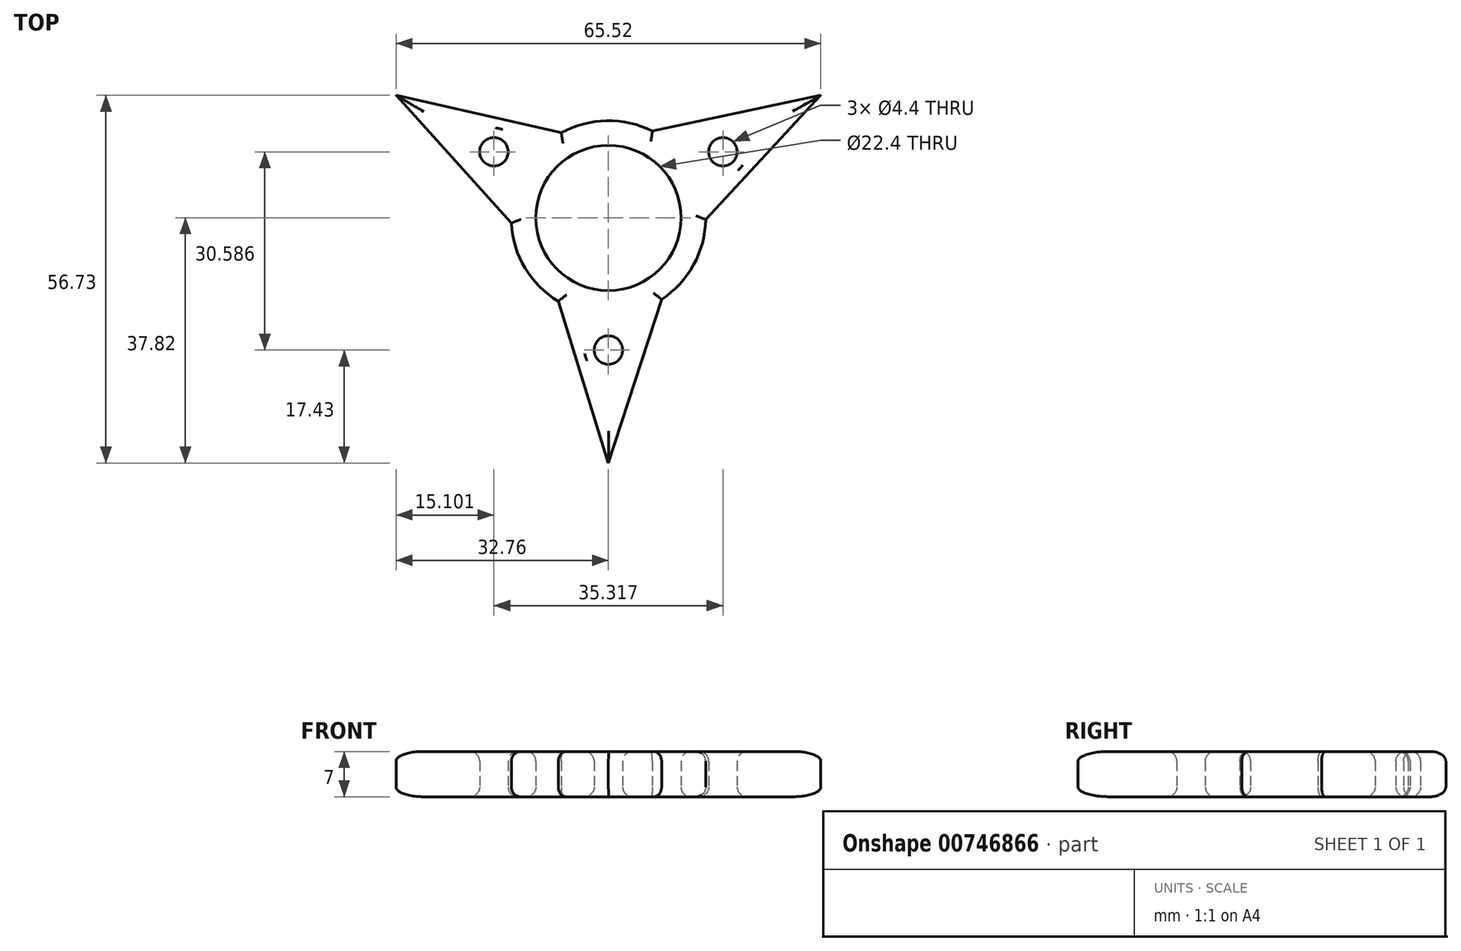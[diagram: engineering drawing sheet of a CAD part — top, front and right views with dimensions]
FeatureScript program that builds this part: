
annotation { "Feature Type Name" : "Feature", "Feature Type Description" : "" }
export const myFeature = defineFeature(function(context is Context, id is Id, definition is map)
    precondition{}
    {
        {
            var Q0;
            Q0=qCreatedBy(makeId("Top.planeOp"),FACE);
            var sketch = newSketch(context, id + "F0", { "sketchPlane" : qUnion([Q0])});
            skCircle(sketch, "E0", {"center": v(0, 0) * mm, "radius": 11.2 * mm});
            skArc(sketch, "E1", {"start": v(-14.98, -0.82) * mm, "mid": v(-12.85, -7.74) * mm, "end": v(-7.73, -12.86) * mm});
            skLineSegment(sketch, "E2", {"start": v(-7.73, -12.86) * mm, "end": v(0, -37.82) * mm});
            skLineSegment(sketch, "E3", {"start": v(0, -37.82) * mm, "end": v(8.2, -12.56) * mm});
            skLineSegment(sketch, "E4.1.0", {"start": v(15, -0.27) * mm, "end": v(32.76, 18.91) * mm});
            skLineSegment(sketch, "E4.1.1", {"start": v(32.76, 18.91) * mm, "end": v(6.78, 13.38) * mm});
            skLineSegment(sketch, "E4.2.0", {"start": v(-7.27, 13.12) * mm, "end": v(-32.76, 18.91) * mm});
            skLineSegment(sketch, "E4.2.1", {"start": v(-32.76, 18.91) * mm, "end": v(-14.98, -0.82) * mm});
            skCircle(sketch, "E5", {"center": v(0, -20.4) * mm, "radius": 2.2 * mm});
            skCircle(sketch, "E6.1.0", {"center": v(17.66, 10.2) * mm, "radius": 2.2 * mm});
            skCircle(sketch, "E6.2.0", {"center": v(-17.66, 10.2) * mm, "radius": 2.2 * mm});
            skArc(sketch, "E7.trimOffspring", {"start": v(8.2, -12.56) * mm, "mid": v(13.13, -7.26) * mm, "end": v(15, -0.27) * mm});
            skArc(sketch, "E8.trimOffspring", {"start": v(6.78, 13.38) * mm, "mid": v(-0.28, 15) * mm, "end": v(-7.27, 13.12) * mm});
            skSolve(sketch);
        }
        {
            var Q0;
            Q0=makeQuery(id+"F0.imprint","IMPRINT",FACE,{"disambiguationData":[TD([[makeQuery(id+"F0.imprint","IMPRINT",EDGE,{"derivedFrom":sQuery(id+"F0.wireOp",EDGE,"E0")}),-1.0]])]});
            extrude(context, id + "F1", {"entities" : qUnion([Q0]), "depth" : 7 * mm, "offsetDistance" : 25 * mm});
        }
        {
            var Q0;
            Q0=makeQuery(id+"F1.opExtrude","CAP_FACE",FACE,{"disambiguationData":[OSD([sQuery(id+"F0.wireOp",EDGE,"E0"),sQuery(id+"F0.wireOp",EDGE,"E1"),sQuery(id+"F0.wireOp",EDGE,"E2"),sQuery(id+"F0.wireOp",EDGE,"E3"),sQuery(id+"F0.wireOp",EDGE,"E4.1.0"),sQuery(id+"F0.wireOp",EDGE,"E4.1.1"),sQuery(id+"F0.wireOp",EDGE,"E4.2.0"),sQuery(id+"F0.wireOp",EDGE,"E4.2.1"),sQuery(id+"F0.wireOp",EDGE,"E5"),sQuery(id+"F0.wireOp",EDGE,"E6.1.0"),sQuery(id+"F0.wireOp",EDGE,"E6.2.0"),sQuery(id+"F0.wireOp",EDGE,"E7.trimOffspring"),sQuery(id+"F0.wireOp",EDGE,"E8.trimOffspring")])],"isStart":false});
            var Q1;
            Q1=makeQuery(id+"F1.opExtrude","CAP_FACE",FACE,{"disambiguationData":[OSD([sQuery(id+"F0.wireOp",EDGE,"E0"),sQuery(id+"F0.wireOp",EDGE,"E1"),sQuery(id+"F0.wireOp",EDGE,"E2"),sQuery(id+"F0.wireOp",EDGE,"E3"),sQuery(id+"F0.wireOp",EDGE,"E4.1.0"),sQuery(id+"F0.wireOp",EDGE,"E4.1.1"),sQuery(id+"F0.wireOp",EDGE,"E4.2.0"),sQuery(id+"F0.wireOp",EDGE,"E4.2.1"),sQuery(id+"F0.wireOp",EDGE,"E5"),sQuery(id+"F0.wireOp",EDGE,"E6.1.0"),sQuery(id+"F0.wireOp",EDGE,"E6.2.0"),sQuery(id+"F0.wireOp",EDGE,"E7.trimOffspring"),sQuery(id+"F0.wireOp",EDGE,"E8.trimOffspring")])],"isStart":true});
            var Q2;
            Q2=makeQuery(id+"F1.opExtrude","CAP_EDGE",EDGE,{"disambiguationData":[OSD([sQuery(id+"F0.wireOp",EDGE,"E2")])],"isStart":true});
            var Q3;
            Q3=makeQuery(id+"F1.opExtrude","CAP_EDGE",EDGE,{"disambiguationData":[OSD([sQuery(id+"F0.wireOp",EDGE,"E1")])],"isStart":true});
            var Q4;
            Q4=makeQuery(id+"F1.opExtrude","CAP_EDGE",EDGE,{"disambiguationData":[OSD([sQuery(id+"F0.wireOp",EDGE,"E4.2.1")])],"isStart":true});
            var Q5;
            Q5=makeQuery(id+"F1.opExtrude","CAP_EDGE",EDGE,{"disambiguationData":[OSD([sQuery(id+"F0.wireOp",EDGE,"E4.2.0")])],"isStart":true});
            var Q6;
            Q6=makeQuery(id+"F1.opExtrude","CAP_EDGE",EDGE,{"disambiguationData":[OSD([sQuery(id+"F0.wireOp",EDGE,"E6.2.0")])],"isStart":true});
            var Q7;
            Q7=makeQuery(id+"F1.opExtrude","CAP_EDGE",EDGE,{"disambiguationData":[OSD([sQuery(id+"F0.wireOp",EDGE,"E5")])],"isStart":true});
            var Q8;
            Q8=makeQuery(id+"F1.opExtrude","CAP_EDGE",EDGE,{"disambiguationData":[OSD([sQuery(id+"F0.wireOp",EDGE,"E6.1.0")])],"isStart":true});
            var Q9;
            Q9=makeQuery(id+"F1.opExtrude","CAP_EDGE",EDGE,{"disambiguationData":[OSD([sQuery(id+"F0.wireOp",EDGE,"E8.trimOffspring")])],"isStart":true});
            var Q10;
            Q10=makeQuery(id+"F1.opExtrude","CAP_EDGE",EDGE,{"disambiguationData":[OSD([sQuery(id+"F0.wireOp",EDGE,"E4.1.1")])],"isStart":true});
            var Q11;
            Q11=makeQuery(id+"F1.opExtrude","CAP_EDGE",EDGE,{"disambiguationData":[OSD([sQuery(id+"F0.wireOp",EDGE,"E4.1.0")])],"isStart":true});
            fillet(context, id + "F2", {"entities" : qUnion([Q0, Q1, Q2, Q3, Q4, Q5, Q6, Q7, Q8, Q9, Q10, Q11]), "radius" : 1.5 * mm, "tangentPropagation" : true, "allowEdgeOverflow" : false});
        }
    });
